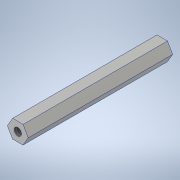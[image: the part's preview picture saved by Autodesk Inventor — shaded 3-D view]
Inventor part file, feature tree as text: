
AUTODESK INVENTOR PART (.ipt)
format: ipt  version: 2021 (Build 250183000, 183)  size: 100,352 bytes
history: native  units: in
note: dims shown in document units (in); Inventor stores cm internally (conversion verified against a paired STEP export)
features: sketch x1, extrude x1, hole x1
ambient origin geometry x8: Origin, YZ Plane, XZ Plane, XY Plane, X Axis, Y Axis, Z Axis, Center Point
bodies: Solid1 (feature_tree)
feature tree (3):
  sketch  "Sketch1"  dims[d0=0.25in d1=2.0in d2=0.0in d3=0.104in d4=2.25in d5=0.375in d6=0.25in d7=0.5635in d8=2.25in d9=0.8108in]
  extrude  "Extrusion1"  Depth=2.0in TaperAngle=0.0deg
  hole  "Hole1"  [1 undecoded]
note: 1 required parameter value undecoded (feature->parameter linkage not recoverable at this tier; creation-order binding heuristic only, values carry confidence <= 0.55)
